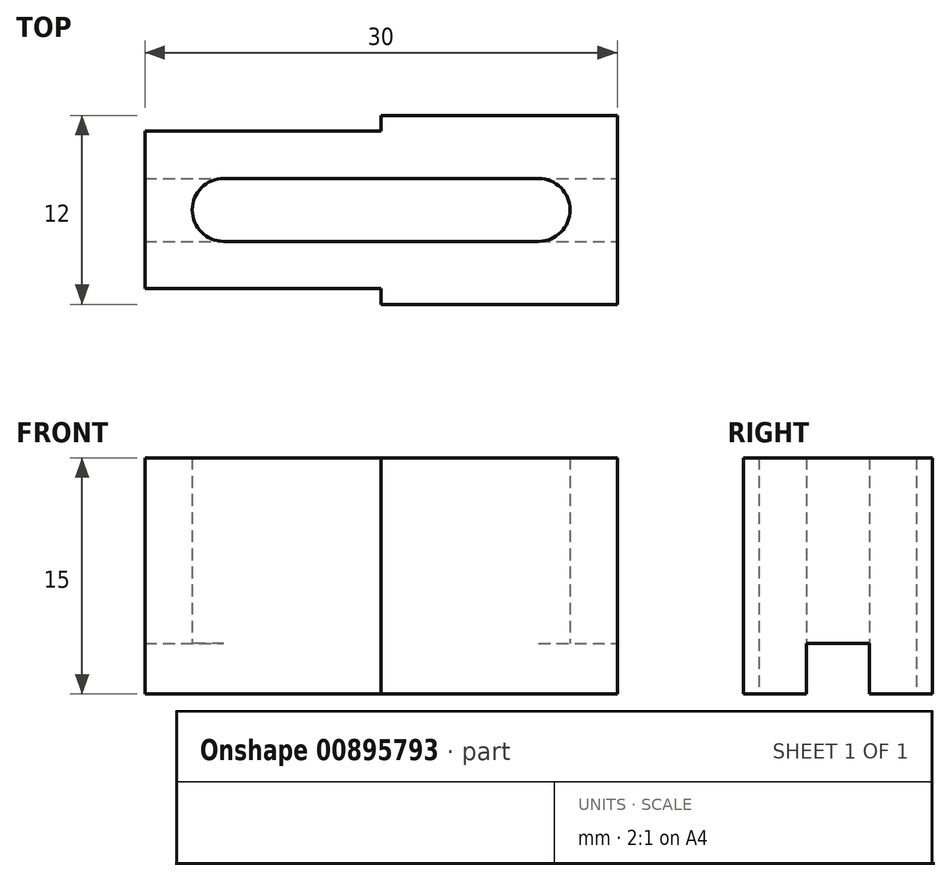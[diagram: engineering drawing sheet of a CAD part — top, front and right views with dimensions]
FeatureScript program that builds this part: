
annotation { "Feature Type Name" : "Feature", "Feature Type Description" : "" }
export const myFeature = defineFeature(function(context is Context, id is Id, definition is map)
    precondition{}
    {
        {
            var Q0;
            Q0=qCreatedBy(makeId("Top.planeOp"),FACE);
            var sketch = newSketch(context, id + "F0", { "sketchPlane" : qUnion([Q0])});
            skLineSegment(sketch, "E0.bottom", {"start": v(-15, 5) * mm, "end": v(0, 5) * mm});
            skLineSegment(sketch, "E0.top", {"start": v(-15, -5) * mm, "end": v(0, -5) * mm});
            skPoint(sketch, "E0.middle", {"position": v(0, 0) * mm});
            skLineSegment(sketch, "E1.bottom", {"start": v(-10, 2) * mm, "end": v(10, 2) * mm});
            skLineSegment(sketch, "E1.top", {"start": v(-10, -2) * mm, "end": v(10, -2) * mm});
            skLineSegment(sketch, "E1.left", {"start": v(-12, 0) * mm, "end": v(-12, 0) * mm});
            skLineSegment(sketch, "E1.right", {"start": v(12, 0) * mm, "end": v(12, 0) * mm});
            skPoint(sketch, "E2.visualSharp", {"position": v(-12, 2) * mm});
            skArc(sketch, "E2.filletArc", {"start": v(-10, 2) * mm, "mid": v(-11.41, 1.41) * mm, "end": v(-12, 0) * mm});
            skPoint(sketch, "E3.visualSharp", {"position": v(-12, -2) * mm});
            skArc(sketch, "E3.filletArc", {"start": v(-12, 0) * mm, "mid": v(-11.41, -1.41) * mm, "end": v(-10, -2) * mm});
            skPoint(sketch, "E4.visualSharp", {"position": v(12, 2) * mm});
            skArc(sketch, "E4.filletArc", {"start": v(12, 0) * mm, "mid": v(11.41, 1.41) * mm, "end": v(10, 2) * mm});
            skPoint(sketch, "E5.visualSharp", {"position": v(12, -2) * mm});
            skArc(sketch, "E5.filletArc", {"start": v(10, -2) * mm, "mid": v(11.41, -1.41) * mm, "end": v(12, 0) * mm});
            skLineSegment(sketch, "E6", {"start": v(0, 5) * mm, "end": v(0, 6) * mm});
            skLineSegment(sketch, "E7", {"start": v(0, 6) * mm, "end": v(15, 6) * mm});
            skLineSegment(sketch, "E8", {"start": v(15, -6) * mm, "end": v(0, -6) * mm});
            skLineSegment(sketch, "E9", {"start": v(0, -6) * mm, "end": v(0, -5) * mm});
            skLineSegment(sketch, "E10", {"start": v(-15, 5) * mm, "end": v(-15, -5) * mm});
            skLineSegment(sketch, "E11", {"start": v(15, 6) * mm, "end": v(15, -6) * mm});
            skSolve(sketch);
        }
        {
            var Q0;
            Q0 = qSketchRegion(id + "F0", true);
            extrude(context, id + "F1", {"entities" : qUnion([Q0]), "depth" : 15 * mm, "offsetDistance" : 25 * mm});
        }
        {
            var Q0;
            Q0=makeQuery(id+"F1.opExtrude","CAP_FACE",FACE,{"disambiguationData":[OSD([sQuery(id+"F0.wireOp",EDGE,"E0.bottom"),sQuery(id+"F0.wireOp",EDGE,"E0.top"),sQuery(id+"F0.wireOp",EDGE,"E1.bottom"),sQuery(id+"F0.wireOp",EDGE,"E1.top"),sQuery(id+"F0.wireOp",EDGE,"E2.filletArc"),sQuery(id+"F0.wireOp",EDGE,"E3.filletArc"),sQuery(id+"F0.wireOp",EDGE,"E4.filletArc"),sQuery(id+"F0.wireOp",EDGE,"E5.filletArc"),sQuery(id+"F0.wireOp",EDGE,"E6"),sQuery(id+"F0.wireOp",EDGE,"E7"),sQuery(id+"F0.wireOp",EDGE,"E8"),sQuery(id+"F0.wireOp",EDGE,"E9"),sQuery(id+"F0.wireOp",EDGE,"E10"),sQuery(id+"F0.wireOp",EDGE,"E11")])],"isStart":true});
            var sketch = newSketch(context, id + "F2", { "sketchPlane" : qUnion([Q0])});
            skLineSegment(sketch, "E12.bottom", {"start": v(-15, 2) * mm, "end": v(15, 2) * mm});
            skLineSegment(sketch, "E12.top", {"start": v(-15, -2) * mm, "end": v(15, -2) * mm});
            skLineSegment(sketch, "E12.left", {"start": v(-15, 2) * mm, "end": v(-15, -2) * mm});
            skLineSegment(sketch, "E12.right", {"start": v(15, 2) * mm, "end": v(15, -2) * mm});
            skPoint(sketch, "E12.middle", {"position": v(0, 0) * mm});
            skSolve(sketch);
        }
        {
            var Q0;
            Q0 = qSketchRegion(id + "F2", true);
            extrude(context, id + "F3", {"entities" : qUnion([Q0]), "operationType" : NewBodyOperationType.REMOVE, "oppositeDirection" : true, "depth" : 3.2 * mm, "offsetDistance" : 25 * mm});
        }
    });
